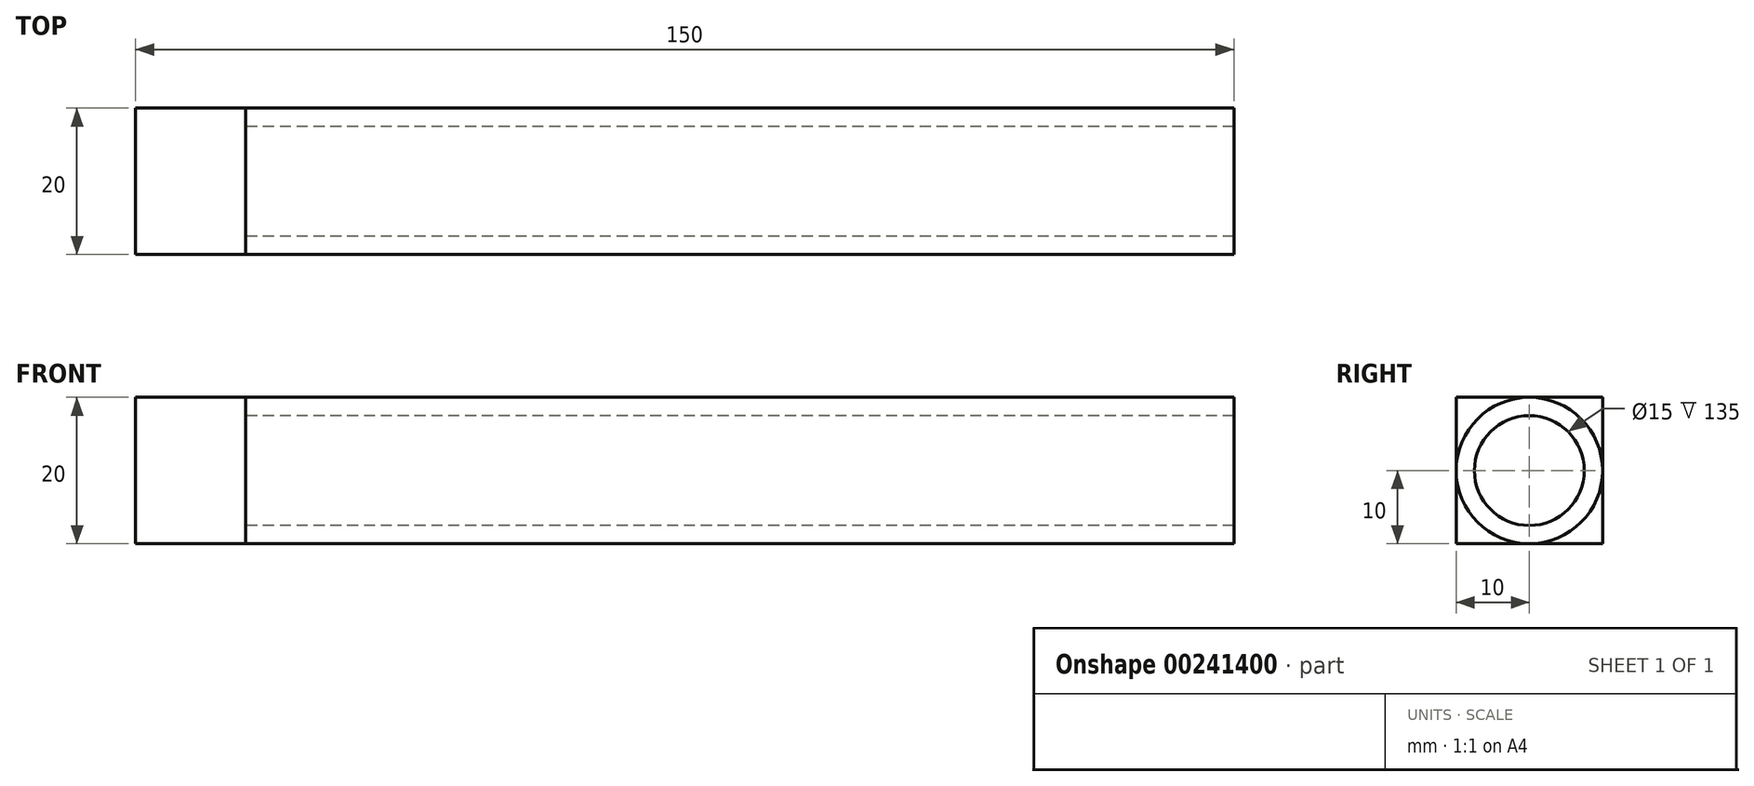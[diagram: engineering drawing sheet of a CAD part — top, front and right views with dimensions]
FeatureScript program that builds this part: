
annotation { "Feature Type Name" : "Feature", "Feature Type Description" : "" }
export const myFeature = defineFeature(function(context is Context, id is Id, definition is map)
    precondition{}
    {
        {
            var Q0;
            Q0=qCreatedBy(makeId("Right.planeOp"),FACE);
            var sketch = newSketch(context, id + "F0", { "sketchPlane" : qUnion([Q0])});
            skLineSegment(sketch, "E0.bottom", {"start": v(-10, 10) * mm, "end": v(10, 10) * mm});
            skLineSegment(sketch, "E0.top", {"start": v(-10, -10) * mm, "end": v(10, -10) * mm});
            skLineSegment(sketch, "E0.left", {"start": v(-10, 10) * mm, "end": v(-10, -10) * mm});
            skLineSegment(sketch, "E0.right", {"start": v(10, 10) * mm, "end": v(10, -10) * mm});
            skPoint(sketch, "E0.middle", {"position": v(0, 0) * mm});
            skSolve(sketch);
        }
        {
            var Q0;
            Q0 = qSketchRegion(id + "F0", true);
            extrude(context, id + "F1", {"entities" : qUnion([Q0]), "depth" : 15 * mm});
        }
        {
            var Q0;
            Q0=makeQuery(id+"F1.opExtrude","CAP_FACE",FACE,{"disambiguationData":[OSD([sQuery(id+"F0.wireOp",EDGE,"E0.bottom"),sQuery(id+"F0.wireOp",EDGE,"E0.top"),sQuery(id+"F0.wireOp",EDGE,"E0.left"),sQuery(id+"F0.wireOp",EDGE,"E0.right")])],"isStart":false});
            var sketch = newSketch(context, id + "F2", { "sketchPlane" : qUnion([Q0])});
            skCircle(sketch, "E1", {"center": v(0, 0) * mm, "radius": 10 * mm});
            skCircle(sketch, "E2", {"center": v(0, 0) * mm, "radius": 7.5 * mm});
            skSolve(sketch);
        }
        {
            var Q0;
            Q0 = qSketchRegion(id + "F2", true);
            extrude(context, id + "F3", {"entities" : qUnion([Q0]), "operationType" : NewBodyOperationType.ADD, "depth" : 135 * mm});
        }
    });
